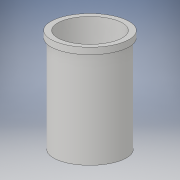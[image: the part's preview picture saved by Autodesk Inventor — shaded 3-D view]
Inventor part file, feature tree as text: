
AUTODESK INVENTOR PART (.ipt)
format: ipt  version: 2018 (Build 220112000, 112)  size: 106,496 bytes
history: native  units: mm
features: revolve x1, sketch x1
ambient origin geometry x8: Origin, YZ Plane, XZ Plane, XY Plane, X Axis, Y Axis, Z Axis, Center Point
bodies: Solid1 (feature_tree)
feature tree (2):
  revolve  "Revolution1"  [1 undecoded]
  sketch  "Sketch1"  dims[d0=40.0mm d1=13.5mm d2=12.0mm d3=14.5mm d4=2.5mm d5=90.0deg]
note: 1 required parameter value undecoded (feature->parameter linkage not recoverable at this tier; creation-order binding heuristic only, values carry confidence <= 0.55)
